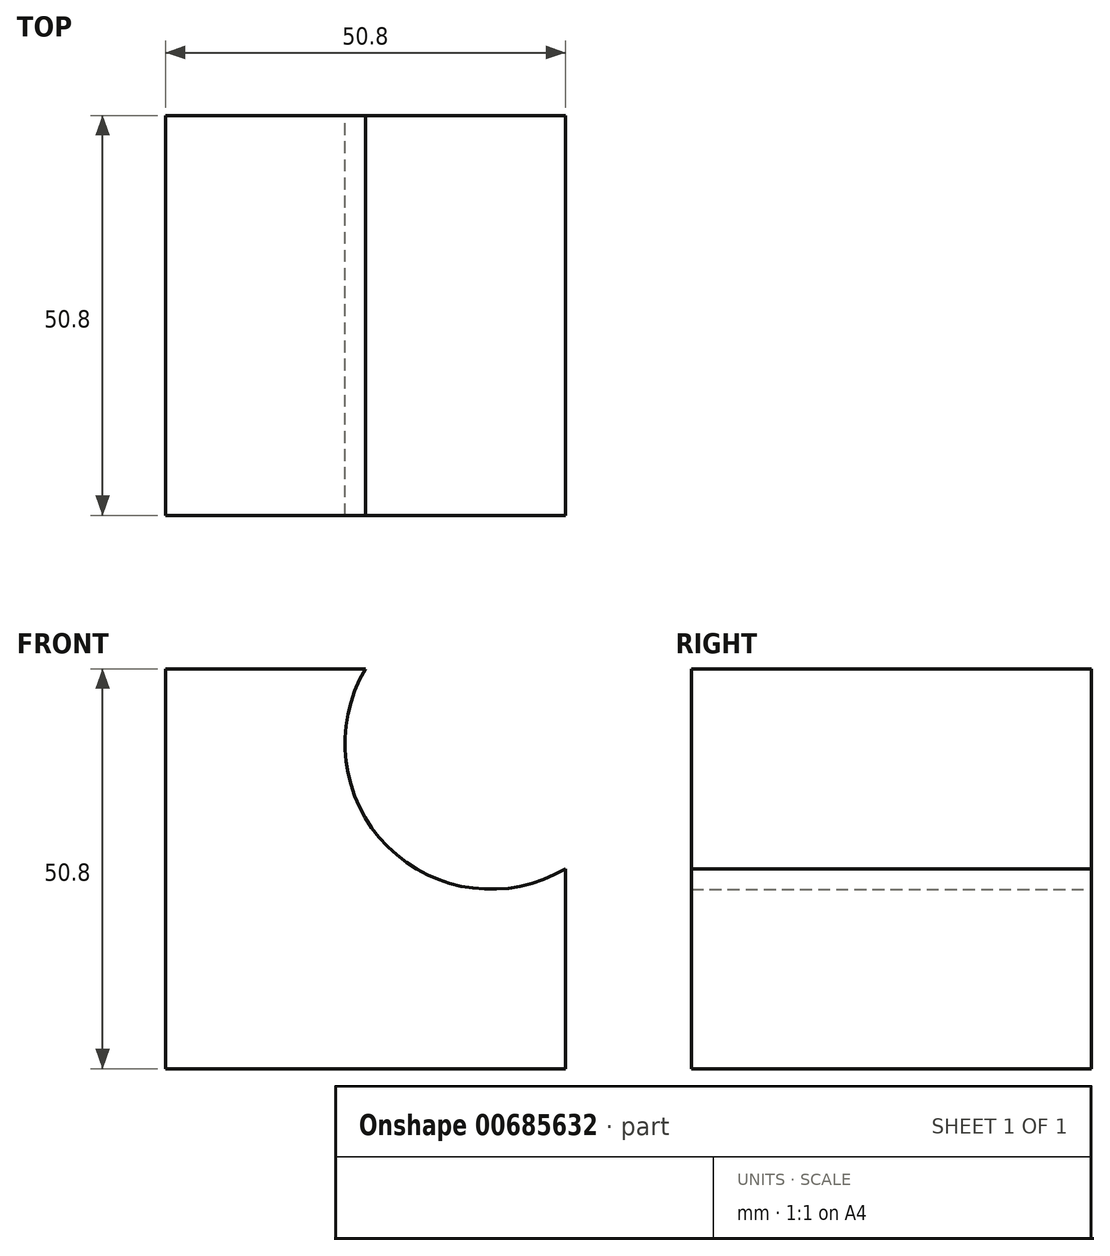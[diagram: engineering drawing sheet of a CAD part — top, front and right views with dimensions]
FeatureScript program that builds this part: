
annotation { "Feature Type Name" : "Feature", "Feature Type Description" : "" }
export const myFeature = defineFeature(function(context is Context, id is Id, definition is map)
    precondition{}
    {
        {
            var Q0;
            Q0=qCreatedBy(makeId("Front.planeOp"),FACE);
            var sketch = newSketch(context, id + "F0", { "sketchPlane" : qUnion([Q0])});
            skLineSegment(sketch, "E0", {"start": v(-44, 26.52) * mm, "end": v(-44, -24.28) * mm});
            skLineSegment(sketch, "E1", {"start": v(-44, -24.28) * mm, "end": v(6.8, -24.28) * mm});
            skLineSegment(sketch, "E2", {"start": v(6.8, -24.28) * mm, "end": v(6.8, 1.12) * mm});
            skLineSegment(sketch, "E3", {"start": v(-44, 26.52) * mm, "end": v(-18.6, 26.52) * mm});
            skArc(sketch, "E4", {"start": v(-18.6, 26.52) * mm, "mid": v(-15.79, 3.94) * mm, "end": v(6.8, 1.12) * mm});
            skSolve(sketch);
        }
        {
            var Q0;
            Q0 = qSketchRegion(id + "F0", true);
            extrude(context, id + "F1", {"entities" : qUnion([Q0]), "depth" : 50.8 * mm, "offsetDistance" : 25.4 * mm});
        }
    });
